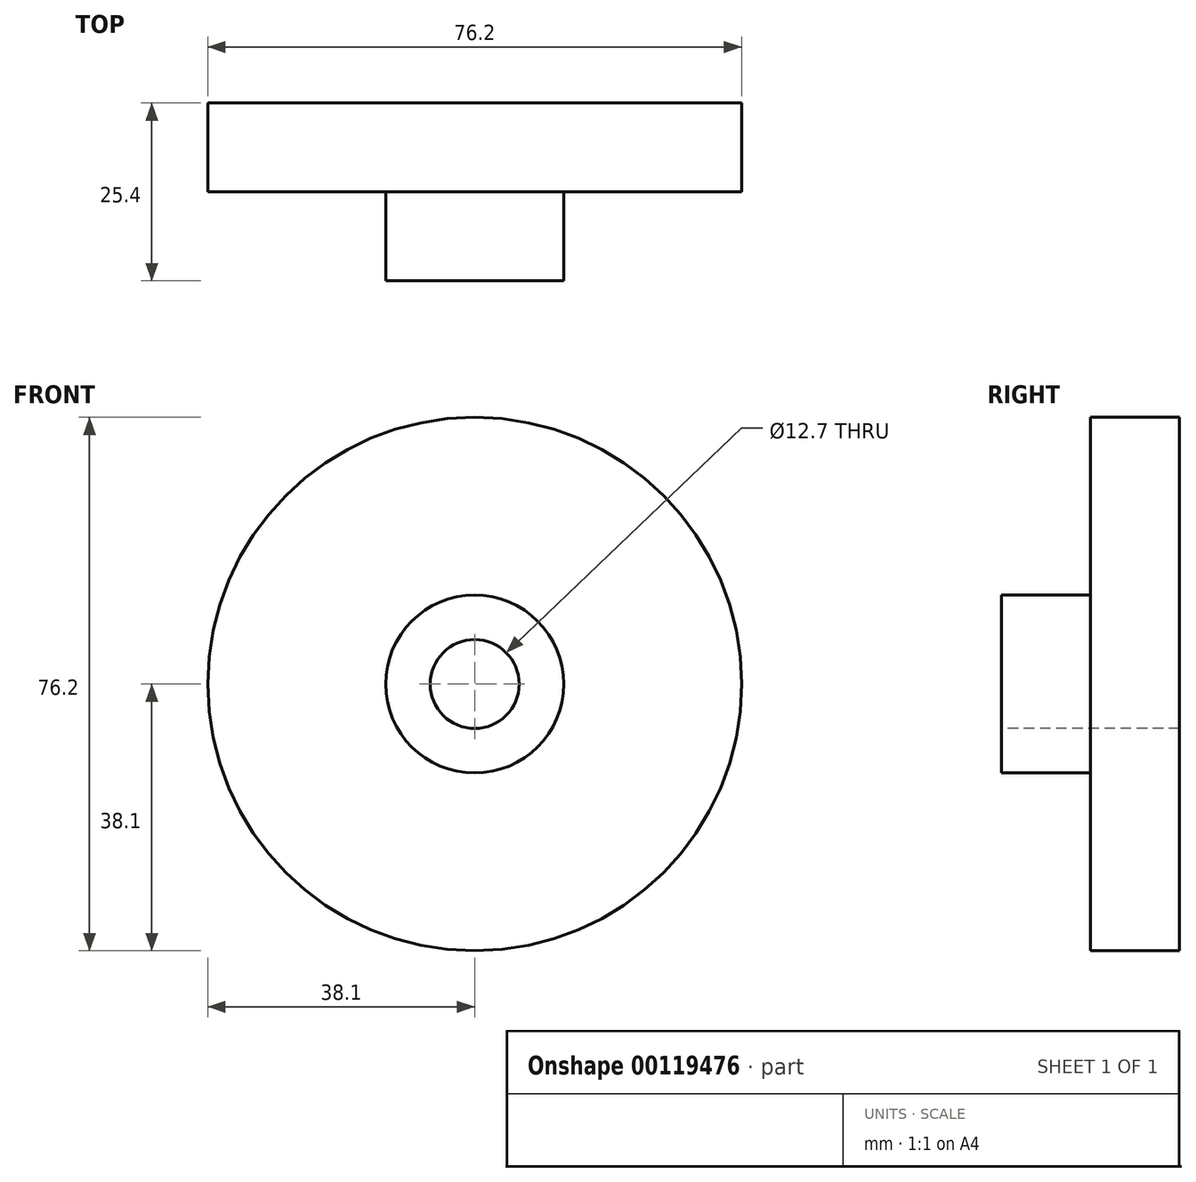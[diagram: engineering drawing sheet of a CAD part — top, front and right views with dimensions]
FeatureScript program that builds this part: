
annotation { "Feature Type Name" : "Feature", "Feature Type Description" : "" }
export const myFeature = defineFeature(function(context is Context, id is Id, definition is map)
    precondition{}
    {
        {
            var Q0;
            Q0=qCreatedBy(makeId("Front.planeOp"),FACE);
            var sketch = newSketch(context, id + "F0", { "sketchPlane" : qUnion([Q0])});
            skCircle(sketch, "E0", {"center": v(0, 0) * mm, "radius": 38.1 * mm});
            skSolve(sketch);
        }
        {
            var Q0;
            Q0=qSketchRegion(id+"F0",true);
            extrude(context, id + "F1", {"entities" : qUnion([Q0]), "depth" : 12.7 * mm});
        }
        {
            var Q0;
            Q0=makeQuery(id+"F1.opExtrude","CAP_FACE",FACE,{"disambiguationData":[OSD([sQuery(id+"F0.wireOp",EDGE,"E0")])],"isStart":false});
            var sketch = newSketch(context, id + "F2", { "sketchPlane" : qUnion([Q0])});
            skCircle(sketch, "E1", {"center": v(0, 0) * mm, "radius": 12.7 * mm});
            skSolve(sketch);
        }
        {
            var Q0;
            Q0=makeQuery(id+"F2.imprint","IMPRINT",FACE,{"disambiguationData":[TD([[makeQuery(id+"F2.imprint","IMPRINT",EDGE,{"derivedFrom":sQuery(id+"F2.wireOp",EDGE,"E1")}),1.0]])]});
            extrude(context, id + "F3", {"entities" : qUnion([Q0]), "operationType" : NewBodyOperationType.ADD, "depth" : 12.7 * mm});
        }
        {
            var Q0;
            Q0=makeQuery(id+"F3.opExtrude","CAP_FACE",FACE,{"disambiguationData":[OSD([sQuery(id+"F2.wireOp",EDGE,"E1")])],"isStart":false});
            var sketch = newSketch(context, id + "F4", { "sketchPlane" : qUnion([Q0])});
            skCircle(sketch, "E2", {"center": v(0, 0) * mm, "radius": 6.35 * mm});
            skSolve(sketch);
        }
        {
            var Q0;
            Q0=makeQuery(id+"F4.imprint","IMPRINT",FACE,{"disambiguationData":[TD([[makeQuery(id+"F4.imprint","IMPRINT",EDGE,{"derivedFrom":sQuery(id+"F4.wireOp",EDGE,"E2")}),1.0]])]});
            var Q1;
            Q1=makeQuery(id+"F1.opExtrude","CAP_FACE",FACE,{"disambiguationData":[OSD([sQuery(id+"F0.wireOp",EDGE,"E0")])],"isStart":true});
            extrude(context, id + "F5", {"entities" : qUnion([Q0]), "operationType" : NewBodyOperationType.REMOVE, "endBound" : BoundingType.UP_TO_SURFACE, "oppositeDirection" : true, "endBoundEntityFace" : qUnion([Q1]), "depth" : 25.4 * mm});
        }
    });
